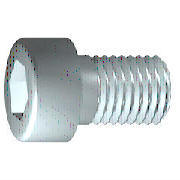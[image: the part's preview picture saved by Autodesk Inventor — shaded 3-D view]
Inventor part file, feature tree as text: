
AUTODESK INVENTOR PART (.ipt)
format: ipt  version: 2018 (Build 220112000, 112)  size: 181,760 bytes
history: native  units: mm (DEFAULTED — no unit token found)
features: sketch x2, extrude x1, plane x1, fillet x1
ambient origin geometry x7: Origin, YZ Plane, XY Plane, X Axis, Y Axis, Z Axis, Center Point
bodies: Solid1 (feature_tree), Body (feature_tree)
feature tree (5):
  extrude  "Slot"  Depth=5.0mm
  plane  "Work Plane1"
  fillet  "Fillet2"  Radius=5.0mm
  sketch  "Sketch1"  dims[d1=22.0mm d2=0.49086mm d3=5.0mm]
  sketch  "Sketch2"  dims[d4=2.5mm d5=60.0deg d6=5.0mm d7=5.0mm d8=4.618802mm d9=8.5mm d10=90.0deg d11=10.0mm d12=0.0mm d13=22.0mm d14=0.0mm d15=0.49076mm d16=0.49076mm d17=0.5mm d19=0.0mm d26=55.0mm d27=45.0deg d28=0.0mm d29=0.0mm d30=0.1mm]
